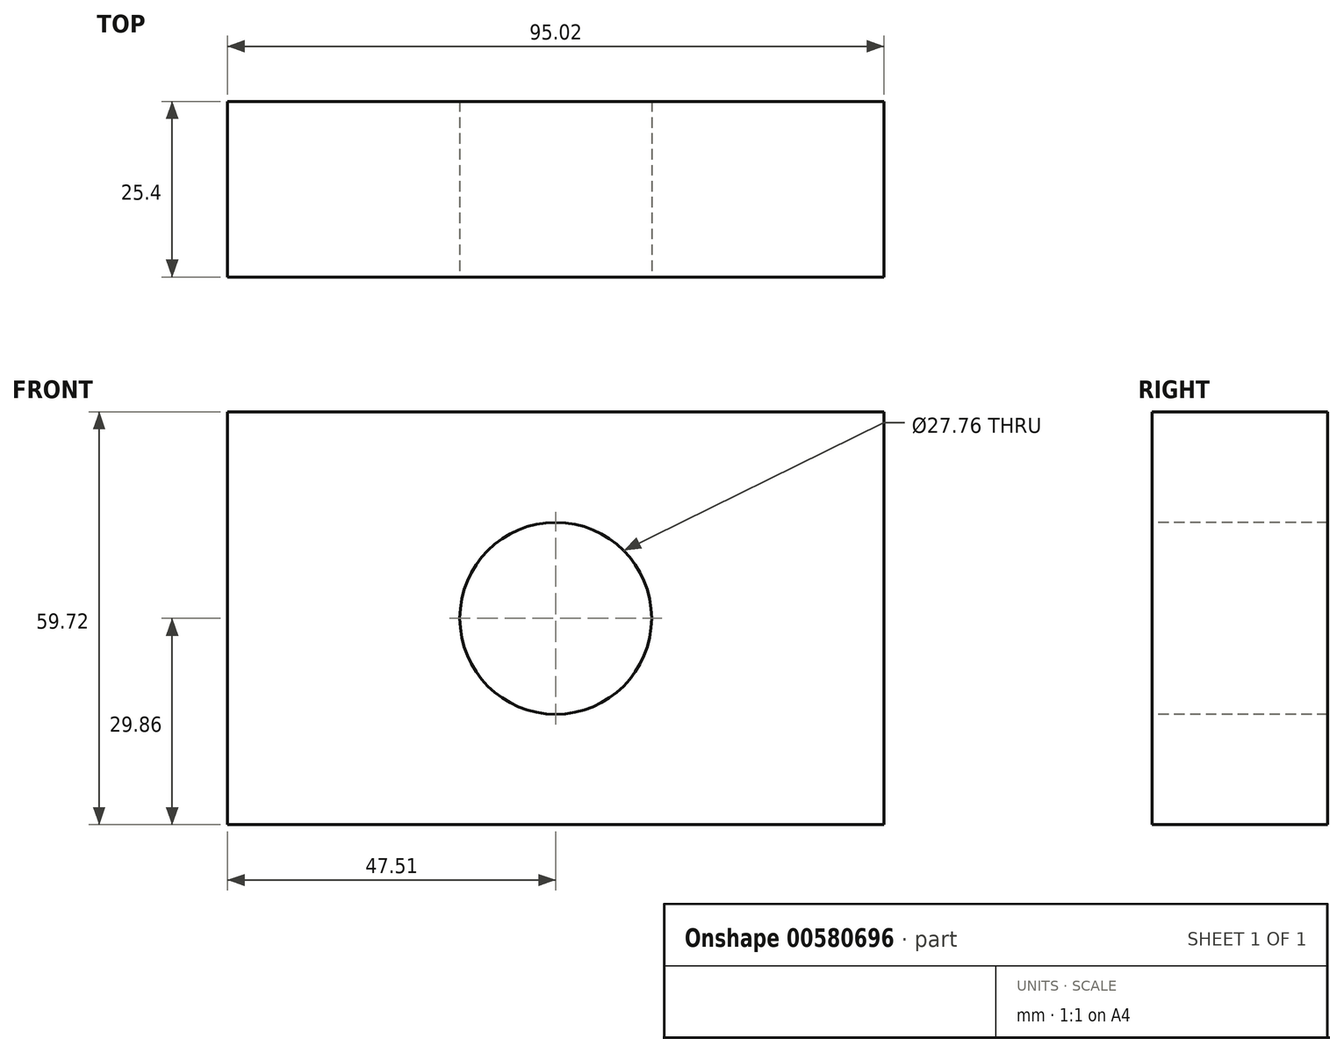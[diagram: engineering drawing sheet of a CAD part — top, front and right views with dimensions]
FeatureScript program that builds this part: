
annotation { "Feature Type Name" : "Feature", "Feature Type Description" : "" }
export const myFeature = defineFeature(function(context is Context, id is Id, definition is map)
    precondition{}
    {
        {
            var Q0;
            Q0=qCreatedBy(makeId("Front.planeOp"),FACE);
            var sketch = newSketch(context, id + "F0", { "sketchPlane" : qUnion([Q0])});
            skLineSegment(sketch, "E0.bottom", {"start": v(47.51, 29.86) * mm, "end": v(-47.51, 29.86) * mm});
            skLineSegment(sketch, "E0.top", {"start": v(47.51, -29.86) * mm, "end": v(-47.51, -29.86) * mm});
            skLineSegment(sketch, "E0.left", {"start": v(47.51, 29.86) * mm, "end": v(47.51, -29.86) * mm});
            skLineSegment(sketch, "E0.right", {"start": v(-47.51, 29.86) * mm, "end": v(-47.51, -29.86) * mm});
            skPoint(sketch, "E0.middle", {"position": v(0, 0) * mm});
            skSolve(sketch);
        }
        {
            var Q0;
            Q0 = qSketchRegion(id + "F0", true);
            extrude(context, id + "F1", {"entities" : qUnion([Q0]), "depth" : 25.4 * mm, "offsetDistance" : 25.4 * mm});
        }
        {
            var Q0;
            Q0=makeQuery(id+"F1.opExtrude","CAP_FACE",FACE,{"disambiguationData":[OSD([sQuery(id+"F0.wireOp",EDGE,"E0.bottom"),sQuery(id+"F0.wireOp",EDGE,"E0.top"),sQuery(id+"F0.wireOp",EDGE,"E0.left"),sQuery(id+"F0.wireOp",EDGE,"E0.right")])],"isStart":false});
            var sketch = newSketch(context, id + "F2", { "sketchPlane" : qUnion([Q0])});
            skCircle(sketch, "E1", {"center": v(0, 0) * mm, "radius": 13.88 * mm});
            skSolve(sketch);
        }
        {
            var Q0;
            Q0 = qSketchRegion(id + "F2", true);
            extrude(context, id + "F3", {"entities" : qUnion([Q0]), "operationType" : NewBodyOperationType.REMOVE, "endBound" : BoundingType.THROUGH_ALL, "oppositeDirection" : true, "depth" : 25.4 * mm, "offsetDistance" : 25.4 * mm});
        }
    });
